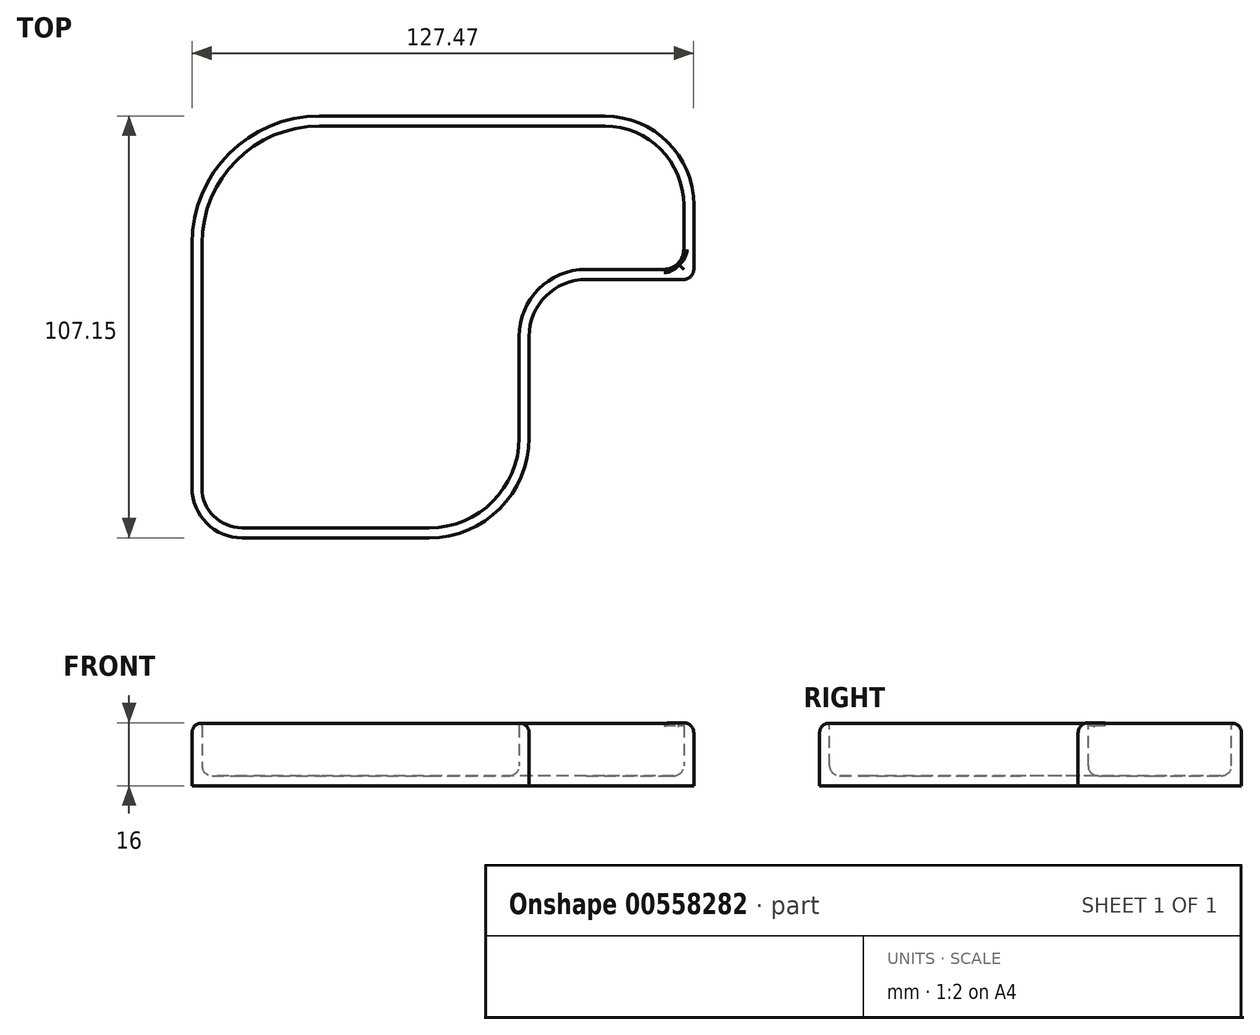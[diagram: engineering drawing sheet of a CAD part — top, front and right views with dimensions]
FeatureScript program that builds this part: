
annotation { "Feature Type Name" : "Feature", "Feature Type Description" : "" }
export const myFeature = defineFeature(function(context is Context, id is Id, definition is map)
    precondition{}
    {
        {
            var Q0;
            Q0=qCreatedBy(makeId("Top.planeOp"),FACE);
            var sketch = newSketch(context, id + "F0", { "sketchPlane" : qUnion([Q0])});
            skLineSegment(sketch, "E0", {"start": v(-101.06, -55.68) * mm, "end": v(-53.5, -55.68) * mm});
            skLineSegment(sketch, "E1", {"start": v(-28.1, -30.28) * mm, "end": v(-28.1, -4.52) * mm});
            skLineSegment(sketch, "E2", {"start": v(-13.6, 9.99) * mm, "end": v(11.17, 9.99) * mm});
            skLineSegment(sketch, "E3", {"start": v(13.71, 12.53) * mm, "end": v(13.71, 28.87) * mm});
            skLineSegment(sketch, "E4", {"start": v(-8.88, 51.47) * mm, "end": v(-81.37, 51.47) * mm});
            skLineSegment(sketch, "E5", {"start": v(-113.76, 19.08) * mm, "end": v(-113.76, -42.98) * mm});
            skPoint(sketch, "E6.visualSharp", {"position": v(-113.76, -55.68) * mm});
            skArc(sketch, "E6.filletArc", {"start": v(-113.76, -42.98) * mm, "mid": v(-110.04, -51.96) * mm, "end": v(-101.06, -55.68) * mm});
            skPoint(sketch, "E7.visualSharp", {"position": v(13.71, 51.47) * mm});
            skArc(sketch, "E7.filletArc", {"start": v(13.71, 28.87) * mm, "mid": v(7.1, 44.85) * mm, "end": v(-8.88, 51.47) * mm});
            skPoint(sketch, "E8.visualSharp", {"position": v(13.71, 9.99) * mm});
            skArc(sketch, "E8.filletArc", {"start": v(11.17, 9.99) * mm, "mid": v(12.97, 10.73) * mm, "end": v(13.71, 12.53) * mm});
            skPoint(sketch, "E9.visualSharp", {"position": v(-28.1, 9.99) * mm});
            skArc(sketch, "E9.filletArc", {"start": v(-13.6, 9.99) * mm, "mid": v(-23.86, 5.74) * mm, "end": v(-28.1, -4.52) * mm});
            skPoint(sketch, "E10.visualSharp", {"position": v(-28.1, -55.68) * mm});
            skArc(sketch, "E10.filletArc", {"start": v(-53.5, -55.68) * mm, "mid": v(-35.55, -48.24) * mm, "end": v(-28.1, -30.28) * mm});
            skPoint(sketch, "E11.visualSharp", {"position": v(-113.76, 51.47) * mm});
            skArc(sketch, "E11.filletArc", {"start": v(-81.37, 51.47) * mm, "mid": v(-104.27, 41.98) * mm, "end": v(-113.76, 19.08) * mm});
            skSolve(sketch);
        }
        {
            var Q0;
            Q0=makeQuery(id+"F0.imprint","IMPRINT",FACE,{"disambiguationData":[TD([[makeQuery(id+"F0.imprint","IMPRINT",EDGE,{"derivedFrom":sQuery(id+"F0.wireOp",EDGE,"E0")}),1.0]])]});
            extrude(context, id + "F1", {"entities" : qUnion([Q0]), "depth" : 16 * mm, "offsetDistance" : 25.4 * mm});
        }
        {
            var Q0;
            Q0=makeQuery(id+"F1.opExtrude","CAP_FACE",FACE,{"disambiguationData":[OSD([sQuery(id+"F0.wireOp",EDGE,"E0"),sQuery(id+"F0.wireOp",EDGE,"E1"),sQuery(id+"F0.wireOp",EDGE,"E2"),sQuery(id+"F0.wireOp",EDGE,"E3"),sQuery(id+"F0.wireOp",EDGE,"E4"),sQuery(id+"F0.wireOp",EDGE,"E5"),sQuery(id+"F0.wireOp",EDGE,"E6.filletArc"),sQuery(id+"F0.wireOp",EDGE,"E7.filletArc"),sQuery(id+"F0.wireOp",EDGE,"E8.filletArc"),sQuery(id+"F0.wireOp",EDGE,"E9.filletArc"),sQuery(id+"F0.wireOp",EDGE,"E10.filletArc"),sQuery(id+"F0.wireOp",EDGE,"E11.filletArc")])],"isStart":false});
            fillet(context, id + "F2", {"entities" : qUnion([Q0]), "radius" : 2.54 * mm, "tangentPropagation" : true, "allowEdgeOverflow" : false});
        }
        {
            var Q0;
            Q0=makeQuery(id+"F1.opExtrude","CAP_FACE",FACE,{"disambiguationData":[OSD([sQuery(id+"F0.wireOp",EDGE,"E0"),sQuery(id+"F0.wireOp",EDGE,"E1"),sQuery(id+"F0.wireOp",EDGE,"E2"),sQuery(id+"F0.wireOp",EDGE,"E3"),sQuery(id+"F0.wireOp",EDGE,"E4"),sQuery(id+"F0.wireOp",EDGE,"E5"),sQuery(id+"F0.wireOp",EDGE,"E6.filletArc"),sQuery(id+"F0.wireOp",EDGE,"E7.filletArc"),sQuery(id+"F0.wireOp",EDGE,"E8.filletArc"),sQuery(id+"F0.wireOp",EDGE,"E9.filletArc"),sQuery(id+"F0.wireOp",EDGE,"E10.filletArc"),sQuery(id+"F0.wireOp",EDGE,"E11.filletArc")])],"isStart":false});
            shell(context, id + "F3", {"entities" : qUnion([Q0]), "thickness" : 2.54 * mm});
        }
        {
            var Q0;
            Q0=makeQuery(id+"F3.opShell","OFFSET_EDGE",EDGE,{"disambiguationData":[OSD([sQuery(id+"F0.wireOp",EDGE,"E2"),sQuery(id+"F0.wireOp",EDGE,"E3"),sQuery(id+"F0.wireOp",EDGE,"E8.filletArc")])]});
            fillet(context, id + "F4", {"entities" : qUnion([Q0]), "radius" : 5.08 * mm, "tangentPropagation" : true, "allowEdgeOverflow" : false});
        }
        {
            var Q0;
            Q0=makeQuery(id+"F3.opShell","OFFSET_EDGE",EDGE,{"disambiguationData":[OSD([sQuery(id+"F0.wireOp",EDGE,"E11.filletArc")])]});
            fillet(context, id + "F5", {"entities" : qUnion([Q0]), "radius" : 2.54 * mm, "tangentPropagation" : true, "allowEdgeOverflow" : false});
        }
        {
            var Q0;
            {var subQ0=sQuery(id+"F0.wireOp",EDGE,"E11.filletArc");var subQ1=makeQuery(id+"F1.opExtrude","CAP_EDGE",EDGE,{"disambiguationData":[OSD([subQ0])],"isStart":false});Q0=makeQuery(id+"F3.opShell","MERGE",EDGE,{"derivedFrom":[makeQuery(id+"F2.opFillet","BLEND_EDGE",EDGE,{"blendedFrom":[subQ1,makeQuery(id+"F1.opExtrude","CAP_FACE",FACE,{"disambiguationData":[OSD([sQuery(id+"F0.wireOp",EDGE,"E0"),sQuery(id+"F0.wireOp",EDGE,"E1"),sQuery(id+"F0.wireOp",EDGE,"E2"),sQuery(id+"F0.wireOp",EDGE,"E3"),sQuery(id+"F0.wireOp",EDGE,"E4"),sQuery(id+"F0.wireOp",EDGE,"E5"),sQuery(id+"F0.wireOp",EDGE,"E6.filletArc"),sQuery(id+"F0.wireOp",EDGE,"E7.filletArc"),sQuery(id+"F0.wireOp",EDGE,"E8.filletArc"),sQuery(id+"F0.wireOp",EDGE,"E9.filletArc"),sQuery(id+"F0.wireOp",EDGE,"E10.filletArc"),subQ0])],"isStart":false})],"blendedInto":[makeQuery(id+"F1.opExtrude","CAP_FACE",FACE,{"disambiguationData":[OSD([sQuery(id+"F0.wireOp",EDGE,"E0"),sQuery(id+"F0.wireOp",EDGE,"E1"),sQuery(id+"F0.wireOp",EDGE,"E2"),sQuery(id+"F0.wireOp",EDGE,"E3"),sQuery(id+"F0.wireOp",EDGE,"E4"),sQuery(id+"F0.wireOp",EDGE,"E5"),sQuery(id+"F0.wireOp",EDGE,"E6.filletArc"),sQuery(id+"F0.wireOp",EDGE,"E7.filletArc"),sQuery(id+"F0.wireOp",EDGE,"E8.filletArc"),sQuery(id+"F0.wireOp",EDGE,"E9.filletArc"),sQuery(id+"F0.wireOp",EDGE,"E10.filletArc"),subQ0])],"isStart":false})]}),makeQuery(id+"F2.opFillet","BLEND_EDGE",EDGE,{"blendedFrom":[subQ1,makeQuery(id+"F1.opExtrude","SWEPT_FACE",FACE,{"disambiguationData":[OSD([subQ0])]})],"blendedInto":[makeQuery(id+"F1.opExtrude","SWEPT_FACE",FACE,{"disambiguationData":[OSD([subQ0])]})]})]});}
            fillet(context, id + "F6", {"entities" : qUnion([Q0]), "radius" : 0.64 * mm, "tangentPropagation" : true, "allowEdgeOverflow" : false});
        }
    });
